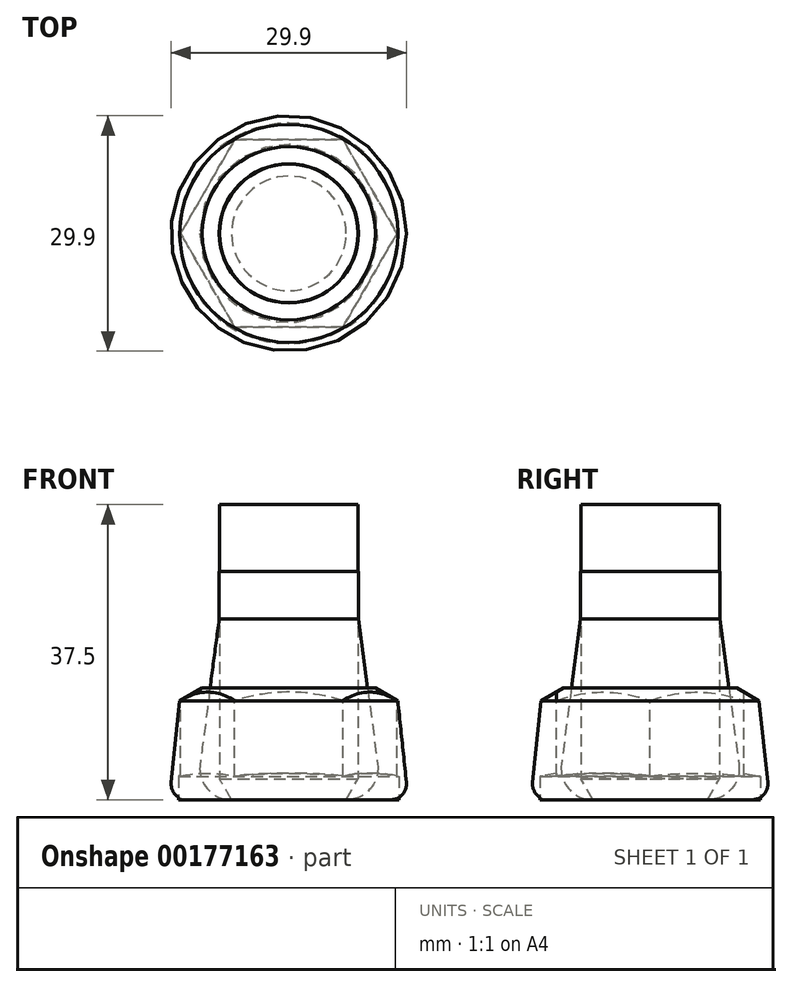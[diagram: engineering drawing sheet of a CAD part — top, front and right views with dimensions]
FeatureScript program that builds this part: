
annotation { "Feature Type Name" : "Feature", "Feature Type Description" : "" }
export const myFeature = defineFeature(function(context is Context, id is Id, definition is map)
    precondition{}
    {
        {
            var Q0;
            Q0=qCreatedBy(makeId("Front.planeOp"),FACE);
            var sketch = newSketch(context, id + "F0", { "sketchPlane" : qUnion([Q0]), "disableImprinting" : false});
            skLineSegment(sketch, "E0", {"start": v(0, 0) * mm, "end": v(0, 14.2) * mm});
            skLineSegment(sketch, "E1", {"start": v(0, 14.2) * mm, "end": v(11, 14.2) * mm});
            skLineSegment(sketch, "E2", {"start": v(13.75, 12.61) * mm, "end": v(13.75, 3.04) * mm});
            skLineSegment(sketch, "E3", {"start": v(13.75, 3.04) * mm, "end": v(14, 3) * mm});
            skLineSegment(sketch, "E4", {"start": v(14, 3) * mm, "end": v(14, 0) * mm});
            skLineSegment(sketch, "E5", {"start": v(14, 0) * mm, "end": v(0, 0) * mm});
            skLineSegment(sketch, "E6", {"start": v(11, 14.2) * mm, "end": v(13.75, 12.61) * mm});
            skLineSegment(sketch, "E7", {"start": v(0, 0) * mm, "end": v(0, 14.2) * mm, "construction": true});
            skSolve(sketch);
        }
        {
            var Q0;
            Q0=qSketchRegion(id+"F0",true);
            var Q1;
            Q1=sQuery(id+"F0.wireOp",EDGE,"E0");
            revolve(context, id + "F1", {"entities" : qUnion([Q0]), "axis" : qUnion([Q1]), "revolveType" : RevolveType.FULL});
        }
        {
            var Q0;
            Q0=makeQuery(id+"F1.opRevolve","SWEPT_FACE",FACE,{"disambiguationData":[OSD([sQuery(id+"F0.wireOp",EDGE,"E1")])]});
            var sketch = newSketch(context, id + "F2", { "sketchPlane" : qUnion([Q0])});
            skCircle(sketch, "E8.cCircle", {"center": v(0, 0) * mm, "radius": 11.9 * mm, "construction": true});
            skLineSegment(sketch, "E8.0", {"start": v(-6.87, 11.9) * mm, "end": v(6.87, 11.9) * mm});
            skLineSegment(sketch, "E8.1", {"start": v(6.87, 11.9) * mm, "end": v(13.74, 0) * mm});
            skLineSegment(sketch, "E8.2", {"start": v(13.74, 0) * mm, "end": v(6.87, -11.9) * mm});
            skLineSegment(sketch, "E8.3", {"start": v(6.87, -11.9) * mm, "end": v(-6.87, -11.9) * mm});
            skLineSegment(sketch, "E8.4", {"start": v(-6.87, -11.9) * mm, "end": v(-13.74, 0) * mm});
            skLineSegment(sketch, "E8.5", {"start": v(-13.74, 0) * mm, "end": v(-6.87, 11.9) * mm});
            skPoint(sketch, "E8.0.midPoint", {"position": v(0, 11.9) * mm});
            skCircle(sketch, "E9", {"center": v(0, 0) * mm, "radius": 23.1 * mm});
            skSolve(sketch);
        }
        {
            var Q0;
            Q0=qSketchRegion(id+"F2",true);
            var Q1;
            Q1=makeQuery(id+"F1.opRevolve","SWEPT_FACE",FACE,{"disambiguationData":[OSD([sQuery(id+"F0.wireOp",EDGE,"E3")])]});
            extrude(context, id + "F3", {"entities" : qUnion([Q0]), "operationType" : NewBodyOperationType.REMOVE, "endBound" : BoundingType.UP_TO_SURFACE, "oppositeDirection" : true, "endBoundEntityFace" : qUnion([Q1]), "depth" : 25 * mm, "offsetDistance" : 25 * mm});
        }
        {
            var Q0;
            Q0=qCreatedBy(makeId("Front.planeOp"),FACE);
            var sketch = newSketch(context, id + "F4", { "sketchPlane" : qUnion([Q0])});
            skLineSegment(sketch, "E10", {"start": v(0, 0) * mm, "end": v(0, 29) * mm});
            skLineSegment(sketch, "E11", {"start": v(0, 29) * mm, "end": v(8.84, 29) * mm});
            skLineSegment(sketch, "E12", {"start": v(8.84, 29) * mm, "end": v(8.84, 23) * mm});
            skLineSegment(sketch, "E13", {"start": v(8.84, 23) * mm, "end": v(11.27, 4.52) * mm});
            skLineSegment(sketch, "E14", {"start": v(7.3, 0) * mm, "end": v(0, 0) * mm});
            skLineSegment(sketch, "E15", {"start": v(0, 0) * mm, "end": v(0, 29) * mm, "construction": true});
            skPoint(sketch, "E16.visualSharp", {"position": v(11.87, 0) * mm});
            skArc(sketch, "E16.filletArc", {"start": v(7.3, 0) * mm, "mid": v(10.31, 1.36) * mm, "end": v(11.27, 4.52) * mm});
            skSolve(sketch);
        }
        {
            var Q0;
            Q0=makeQuery(id+"F4.imprint","IMPRINT",FACE,{"disambiguationData":[TD([[makeQuery(id+"F4.imprint","IMPRINT",EDGE,{"derivedFrom":sQuery(id+"F4.wireOp",EDGE,"E10")}),-1.0]])]});
            var Q1;
            Q1=sQuery(id+"F4.wireOp",EDGE,"E10");
            revolve(context, id + "F5", {"surfaceOperationType" : NewSurfaceOperationType.NEW, "entities" : qUnion([Q0]), "axis" : qUnion([Q1]), "revolveType" : RevolveType.FULL});
        }
        {
            var Q0;
            Q0=qCreatedBy(makeId("Front.planeOp"),FACE);
            var sketch = newSketch(context, id + "F6", { "sketchPlane" : qUnion([Q0])});
            skLineSegment(sketch, "E17", {"start": v(0, 0) * mm, "end": v(0, 14.2) * mm, "construction": true});
            skLineSegment(sketch, "E18", {"start": v(0, 14.2) * mm, "end": v(11, 14.2) * mm});
            skLineSegment(sketch, "E19", {"start": v(11, 14.2) * mm, "end": v(13.85, 12.55) * mm});
            skLineSegment(sketch, "E20", {"start": v(13.85, 12.55) * mm, "end": v(14.94, 2.2) * mm});
            skLineSegment(sketch, "E21", {"start": v(12.95, 0) * mm, "end": v(0, 0) * mm});
            skLineSegment(sketch, "E22", {"start": v(0, 14.2) * mm, "end": v(0, 0) * mm});
            skPoint(sketch, "E23.visualSharp", {"position": v(15.17, 0) * mm});
            skArc(sketch, "E23.filletArc", {"start": v(12.95, 0) * mm, "mid": v(14.43, 0.66) * mm, "end": v(14.94, 2.2) * mm});
            skSolve(sketch);
        }
        {
            var Q0;
            Q0 = qSketchRegion(id + "F6", true);
            var Q1;
            Q1=sQuery(id+"F6.wireOp",EDGE,"E22");
            revolve(context, id + "F7", {"surfaceOperationType" : NewSurfaceOperationType.NEW, "entities" : qUnion([Q0]), "axis" : qUnion([Q1]), "revolveType" : RevolveType.FULL});
        }
        {
            var Q0;
            Q0=qCreatedBy(makeId("Front.planeOp"),FACE);
            var sketch = newSketch(context, id + "F8", { "sketchPlane" : qUnion([Q0])});
            skLineSegment(sketch, "E24", {"start": v(0, 0) * mm, "end": v(0, 37.5) * mm});
            skLineSegment(sketch, "E25", {"start": v(0, 37.5) * mm, "end": v(8.8, 37.5) * mm});
            skLineSegment(sketch, "E26", {"start": v(8.8, 37.5) * mm, "end": v(8.8, 2.64) * mm});
            skLineSegment(sketch, "E27", {"start": v(8.8, 2.64) * mm, "end": v(7.28, 0) * mm});
            skLineSegment(sketch, "E28", {"start": v(7.28, 0) * mm, "end": v(0, 0) * mm});
            skLineSegment(sketch, "E29", {"start": v(0, 37.5) * mm, "end": v(0, 0) * mm, "construction": true});
            skSolve(sketch);
        }
        {
            var Q0;
            Q0 = qSketchRegion(id + "F8", true);
            var Q1;
            Q1=sQuery(id+"F8.wireOp",EDGE,"E24");
            revolve(context, id + "F9", {"surfaceOperationType" : NewSurfaceOperationType.NEW, "entities" : qUnion([Q0]), "axis" : qUnion([Q1]), "revolveType" : RevolveType.FULL});
        }
    });
